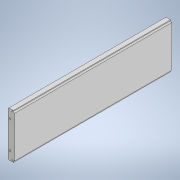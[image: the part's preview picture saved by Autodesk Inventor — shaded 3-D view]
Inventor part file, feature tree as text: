
AUTODESK INVENTOR PART (.ipt)
format: ipt  version: 2022.2 (Build 262287010, 287A)  size: 122,368 bytes
history: native  units: mm
features: extrude x1, sketch x1
ambient origin geometry x8: Origin, YZ Plane, XZ Plane, XY Plane, X Axis, Y Axis, Z Axis, Center Point
bodies: Volumenkörper1 (feature_tree)
feature tree (2):
  extrude  "Extrusion1"  Depth=12.5mm
  sketch  "Skizze1"  dims[d0=3.2mm d1=12.5mm d2=86.0mm d3=16.5mm d4=16.5mm d5=3.8mm d6=1.4mm d7=2.5mm d8=5.2mm d9=1.5mm d10=1.8mm d11=5.2mm d12=1.8mm d14=2.5mm d15=2.0mm d16=300.0mm d17=0.0mm]
